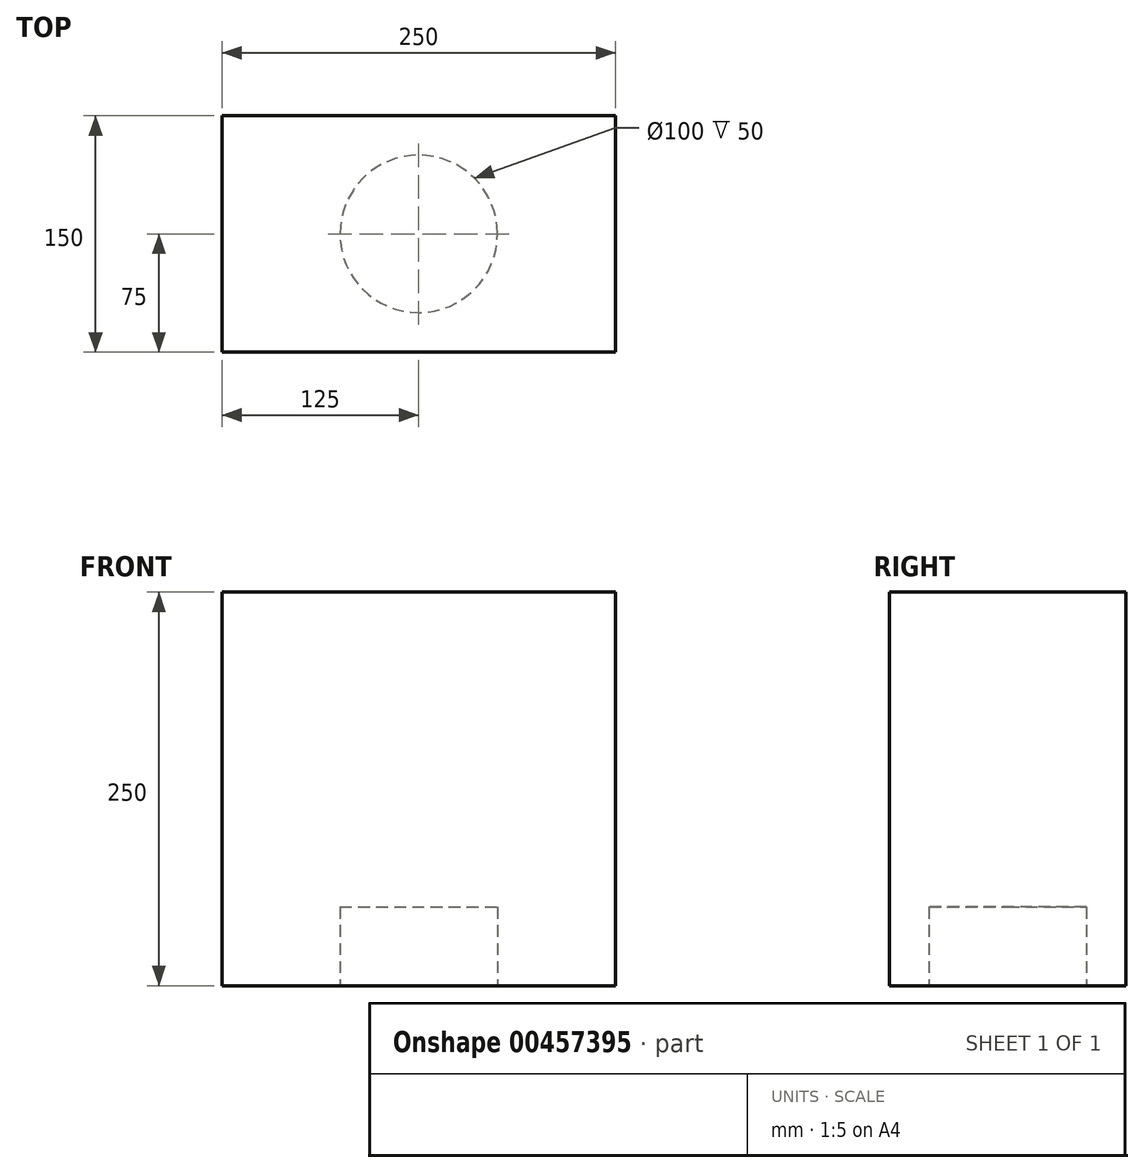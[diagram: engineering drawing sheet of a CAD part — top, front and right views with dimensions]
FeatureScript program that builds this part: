
annotation { "Feature Type Name" : "Feature", "Feature Type Description" : "" }
export const myFeature = defineFeature(function(context is Context, id is Id, definition is map)
    precondition{}
    {
        {
            var Q0;
            Q0=qCreatedBy(makeId("Front.planeOp"),FACE);
            var sketch = newSketch(context, id + "F0", { "sketchPlane" : qUnion([Q0])});
            skLineSegment(sketch, "E0.bottom", {"start": v(100, -100) * mm, "end": v(-100, -100) * mm});
            skLineSegment(sketch, "E0.top", {"start": v(100, 100) * mm, "end": v(-100, 100) * mm});
            skLineSegment(sketch, "E0.left", {"start": v(100, -100) * mm, "end": v(100, 100) * mm});
            skLineSegment(sketch, "E0.right", {"start": v(-100, -100) * mm, "end": v(-100, 100) * mm});
            skPoint(sketch, "E0.middle", {"position": v(0, 0) * mm});
            skSolve(sketch);
        }
        {
            var Q0;
            Q0=makeQuery(id+"F0.imprint","IMPRINT",FACE,{"disambiguationData":[TD([[makeQuery(id+"F0.imprint","IMPRINT",EDGE,{"derivedFrom":sQuery(id+"F0.wireOp",EDGE,"E0.bottom")}),-1.0]])]});
            extrude(context, id + "F1", {"entities" : qUnion([Q0]), "oppositeDirection" : true, "depth" : 100 * mm});
        }
        {
            var Q0;
            Q0=makeQuery(id+"F1.opExtrude","CAP_FACE",FACE,{"disambiguationData":[OSD([sQuery(id+"F0.wireOp",EDGE,"E0.bottom"),sQuery(id+"F0.wireOp",EDGE,"E0.top"),sQuery(id+"F0.wireOp",EDGE,"E0.left"),sQuery(id+"F0.wireOp",EDGE,"E0.right")])],"isStart":true});
            cPlane(context, id + "F2", {"entities" : qUnion([Q0]), "cplaneType" : CPlaneType.OFFSET, "offset" : 25 * mm, "width" : 150 * mm, "height" : 150 * mm});
        }
        {
            var Q0;
            Q0=qCreatedBy(id+"F2.planeOp",FACE);
            var sketch = newSketch(context, id + "F3", { "sketchPlane" : qUnion([Q0])});
            skLineSegment(sketch, "E1.bottom", {"start": v(125, -125) * mm, "end": v(-125, -125) * mm});
            skLineSegment(sketch, "E1.top", {"start": v(125, 125) * mm, "end": v(-125, 125) * mm});
            skLineSegment(sketch, "E1.left", {"start": v(125, -125) * mm, "end": v(125, 125) * mm});
            skLineSegment(sketch, "E1.right", {"start": v(-125, -125) * mm, "end": v(-125, 125) * mm});
            skPoint(sketch, "E1.middle", {"position": v(0, 0) * mm});
            skSolve(sketch);
        }
        {
            var Q0;
            Q0=makeQuery(id+"F3.imprint","IMPRINT",FACE,{"disambiguationData":[TD([[makeQuery(id+"F3.imprint","IMPRINT",EDGE,{"derivedFrom":sQuery(id+"F3.wireOp",EDGE,"E1.bottom")}),-1.0]])]});
            extrude(context, id + "F4", {"entities" : qUnion([Q0]), "operationType" : NewBodyOperationType.ADD, "oppositeDirection" : true, "depth" : 150 * mm});
        }
        {
            var Q0;
            Q0=makeQuery(id+"F4.opExtrude","SWEPT_FACE",FACE,{"disambiguationData":[OSD([sQuery(id+"F3.wireOp",EDGE,"E1.bottom")])]});
            var sketch = newSketch(context, id + "F5", { "sketchPlane" : qUnion([Q0])});
            skPoint(sketch, "E2.endSnap0", {"position": v(0, -125) * mm});
            skCircle(sketch, "E3", {"center": v(0, -50) * mm, "radius": 50 * mm});
            skSolve(sketch);
        }
        {
            var Q0;
            Q0=makeQuery(id+"F5.imprint","IMPRINT",FACE,{"disambiguationData":[TD([[makeQuery(id+"F5.imprint","IMPRINT",EDGE,{"derivedFrom":sQuery(id+"F5.wireOp",EDGE,"E3")}),1.0]])]});
            extrude(context, id + "F6", {"entities" : qUnion([Q0]), "operationType" : NewBodyOperationType.REMOVE, "oppositeDirection" : true, "depth" : 50 * mm});
        }
    });
